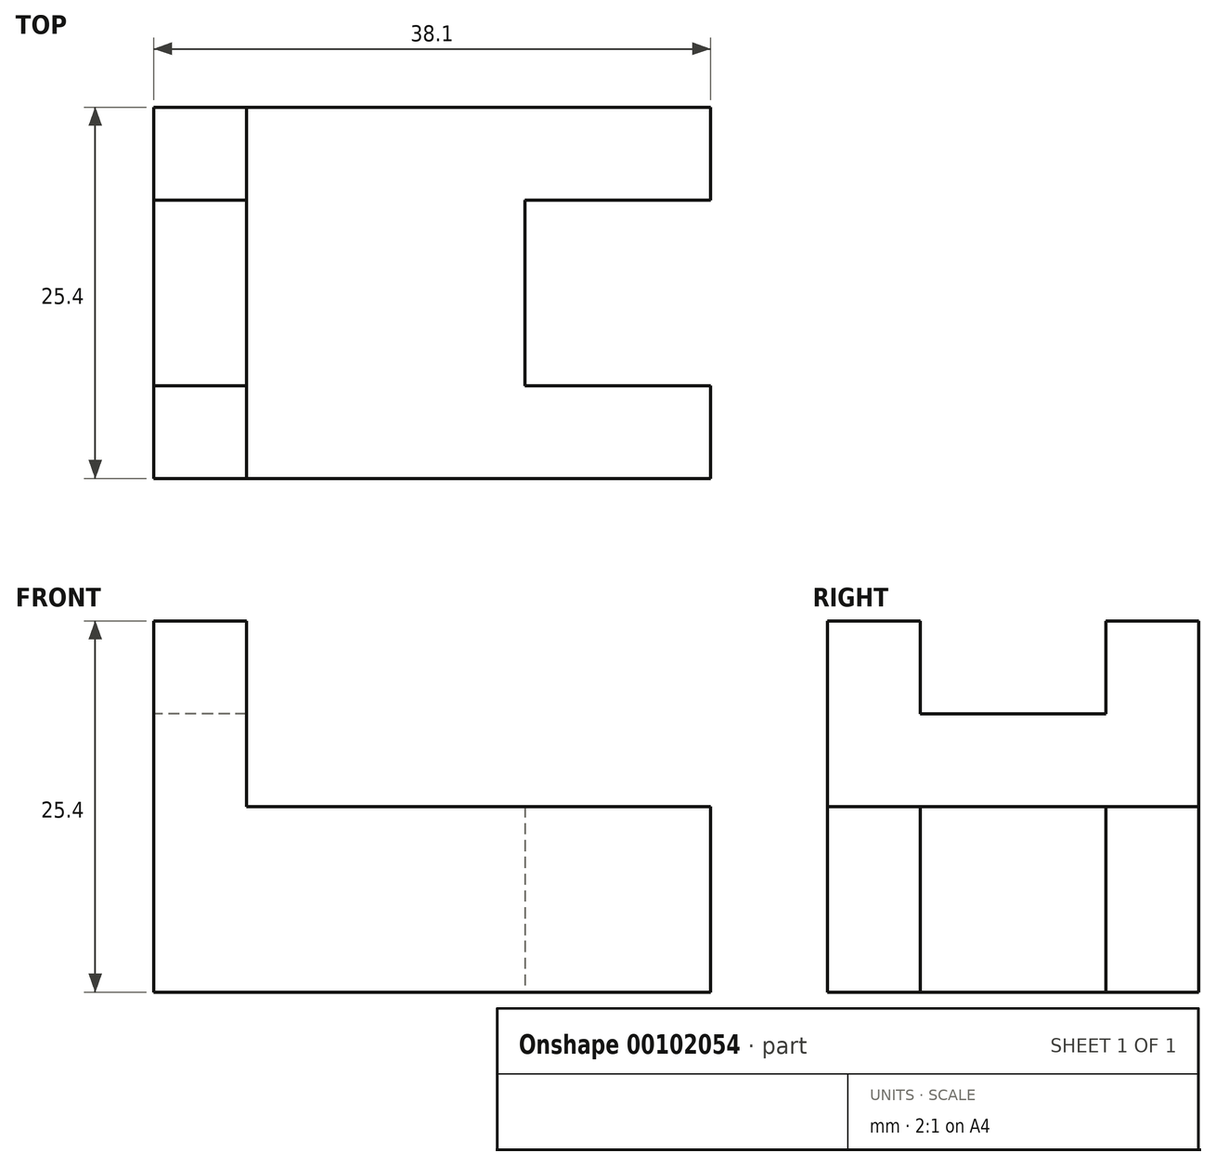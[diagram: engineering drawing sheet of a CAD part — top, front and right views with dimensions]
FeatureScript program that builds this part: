
annotation { "Feature Type Name" : "Feature", "Feature Type Description" : "" }
export const myFeature = defineFeature(function(context is Context, id is Id, definition is map)
    precondition{}
    {
        {
            var Q0;
            Q0=qCreatedBy(makeId("Front.planeOp"),FACE);
            var sketch = newSketch(context, id + "F0", { "sketchPlane" : qUnion([Q0])});
            skLineSegment(sketch, "E0", {"start": v(0, 0) * mm, "end": v(0, 25.4) * mm});
            skLineSegment(sketch, "E1", {"start": v(0, 25.4) * mm, "end": v(6.35, 25.4) * mm});
            skLineSegment(sketch, "E2", {"start": v(6.35, 25.4) * mm, "end": v(6.35, 12.7) * mm});
            skLineSegment(sketch, "E3", {"start": v(6.35, 12.7) * mm, "end": v(38.1, 12.7) * mm});
            skLineSegment(sketch, "E4", {"start": v(38.1, 12.7) * mm, "end": v(38.1, 0) * mm});
            skLineSegment(sketch, "E5", {"start": v(38.1, 0) * mm, "end": v(0, 0) * mm});
            skSolve(sketch);
        }
        {
            var Q0;
            Q0=makeQuery(id+"F0.imprint","IMPRINT",FACE,{"disambiguationData":[TD([[makeQuery(id+"F0.imprint","IMPRINT",EDGE,{"derivedFrom":sQuery(id+"F0.wireOp",EDGE,"E0")}),-1.0]])]});
            extrude(context, id + "F1", {"entities" : qUnion([Q0]), "depth" : 25.4 * mm});
        }
        {
            var Q0;
            Q0=qCreatedBy(makeId("Right.planeOp"),FACE);
            var sketch = newSketch(context, id + "F2", { "sketchPlane" : qUnion([Q0])});
            skLineSegment(sketch, "E6", {"start": v(-19.05, 25.4) * mm, "end": v(-19.05, 19.05) * mm});
            skLineSegment(sketch, "E7", {"start": v(-19.05, 19.05) * mm, "end": v(-6.35, 19.05) * mm});
            skLineSegment(sketch, "E8", {"start": v(-6.35, 19.05) * mm, "end": v(-6.35, 25.4) * mm});
            skLineSegment(sketch, "E9", {"start": v(-6.35, 25.4) * mm, "end": v(-19.05, 25.4) * mm});
            skSolve(sketch);
        }
        {
            var Q0;
            Q0=makeQuery(id+"F2.imprint","IMPRINT",FACE,{"disambiguationData":[TD([[makeQuery(id+"F2.imprint","IMPRINT",EDGE,{"derivedFrom":sQuery(id+"F2.wireOp",EDGE,"E6")}),1.0]])]});
            extrude(context, id + "F3", {"entities" : qUnion([Q0]), "operationType" : NewBodyOperationType.REMOVE, "depth" : 25.4 * mm});
        }
        {
            var Q0;
            Q0=qCreatedBy(makeId("Top.planeOp"),FACE);
            var sketch = newSketch(context, id + "F4", { "sketchPlane" : qUnion([Q0])});
            skLineSegment(sketch, "E10", {"start": v(38.1, -6.35) * mm, "end": v(25.4, -6.35) * mm});
            skLineSegment(sketch, "E11", {"start": v(25.4, -6.35) * mm, "end": v(25.4, -19.05) * mm});
            skLineSegment(sketch, "E12", {"start": v(25.4, -19.05) * mm, "end": v(38.1, -19.05) * mm});
            skLineSegment(sketch, "E13", {"start": v(38.1, -19.05) * mm, "end": v(38.1, -6.35) * mm});
            skSolve(sketch);
        }
        {
            var Q0;
            Q0 = qSketchRegion(id + "F4", true);
            extrude(context, id + "F5", {"entities" : qUnion([Q0]), "operationType" : NewBodyOperationType.REMOVE, "depth" : 25.4 * mm});
        }
    });
